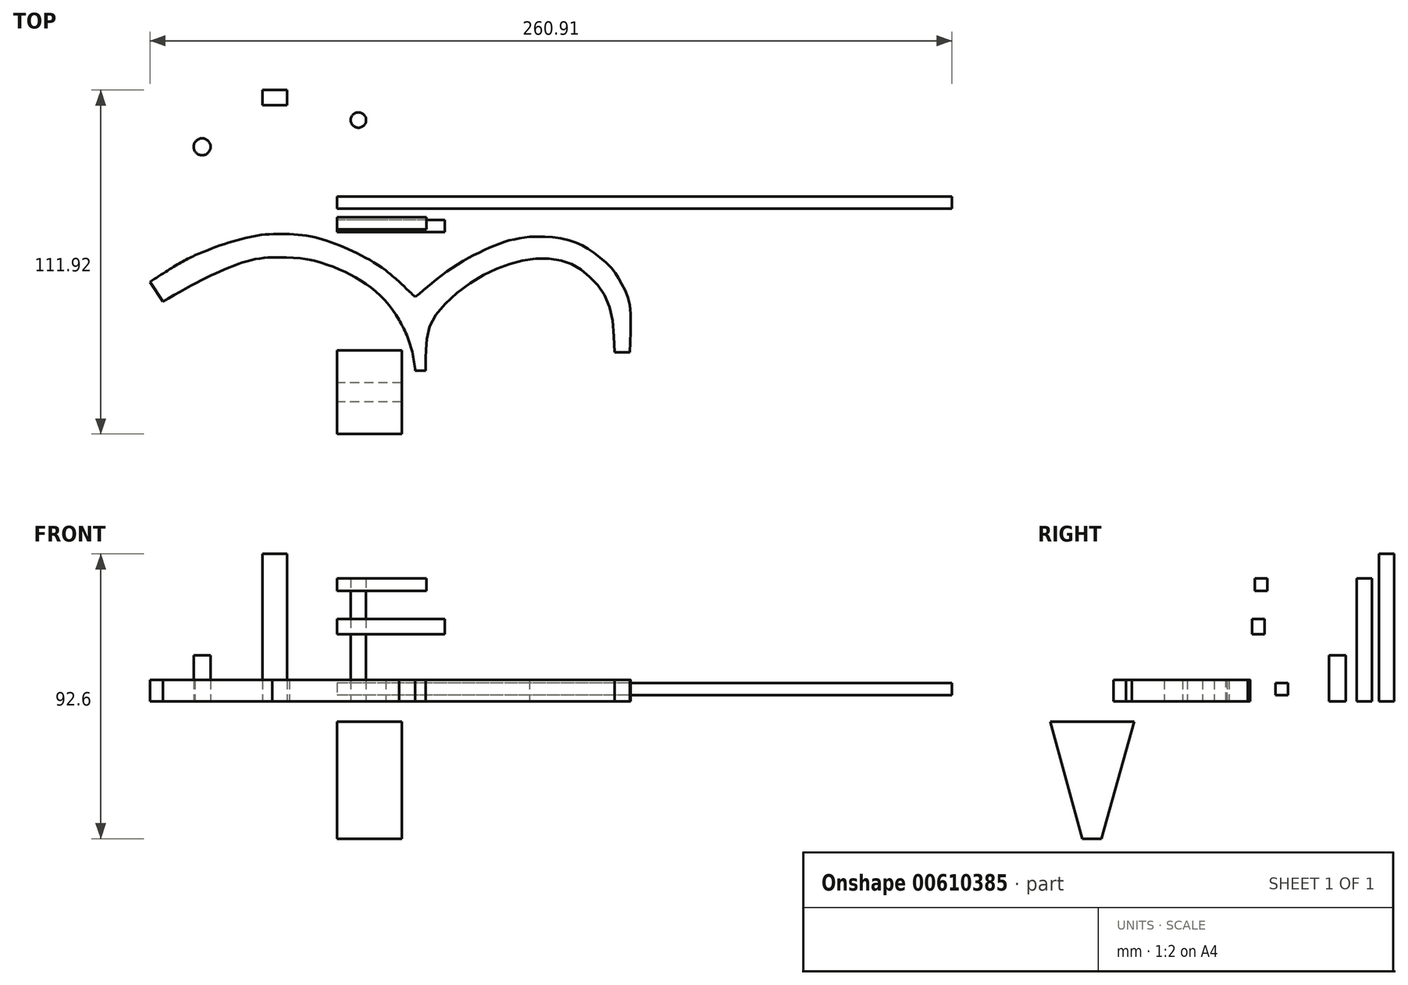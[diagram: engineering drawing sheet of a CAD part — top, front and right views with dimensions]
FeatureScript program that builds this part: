
annotation { "Feature Type Name" : "Feature", "Feature Type Description" : "" }
export const myFeature = defineFeature(function(context is Context, id is Id, definition is map)
    precondition{}
    {
        {
            var Q0;
            Q0=qCreatedBy(makeId("Top.planeOp"),FACE);
            var sketch = newSketch(context, id + "F0", { "sketchPlane" : qUnion([Q0])});
            skFitSpline(sketch, "E0", {"points": [v(-60.91, -6.53) * mm, v(-54.5, -2.45) * mm, v(-50.14, 0.16) * mm, v(-46.25, 2.14) * mm], "startDerivative": vector(16.01, 10.57) * mm, "endDerivative": vector(13, 6.35) * mm});
            skFitSpline(sketch, "E1", {"points": [v(-46.25, 2.14) * mm, v(-37.97, 5.34) * mm, v(-29.58, 7.82) * mm, v(-22.67, 8.93) * mm, v(-15.55, 8.98) * mm], "startDerivative": vector(30.88, 12.56) * mm, "endDerivative": vector(30.39, -0.7) * mm});
            skFitSpline(sketch, "E2", {"points": [v(-15.55, 8.98) * mm, v(-9.55, 8.46) * mm, v(-3.97, 7.07) * mm, v(2.6, 4.6) * mm, v(9.53, 1.22) * mm, v(15.8, -2.7) * mm], "startDerivative": vector(32.42, -1.74) * mm, "endDerivative": vector(29.3, -20.88) * mm});
            skFitSpline(sketch, "E3", {"points": [v(15.8, -2.7) * mm, v(20.28, -6.6) * mm, v(25.42, -11.43) * mm], "startDerivative": vector(8.02, -7.35) * mm, "endDerivative": vector(10.95, -9.58) * mm});
            skFitSpline(sketch, "E4", {"points": [v(25.42, -11.43) * mm, v(31.57, -6.35) * mm, v(40.36, -0.1) * mm, v(48.65, 4.16) * mm, v(55.71, 6.87) * mm, v(62.61, 8.1) * mm], "startDerivative": vector(29.98, 25.4) * mm, "endDerivative": vector(38.2, 5.06) * mm});
            skFitSpline(sketch, "E5", {"points": [v(62.61, 8.1) * mm, v(68.78, 8.1) * mm, v(75.88, 6.87) * mm, v(80.74, 4.76) * mm, v(85.37, 1.55) * mm, v(89.92, -2.86) * mm, v(92.1, -6.3) * mm, v(94.56, -11.43) * mm, v(95.53, -18.9) * mm, v(95.15, -29.45) * mm], "startDerivative": vector(54.77, 2.08) * mm, "endDerivative": vector(-4.35, -75.98) * mm});
            skFitSpline(sketch, "E6", {"points": [v(95.15, -29.45) * mm, v(90.25, -29.45) * mm], "startDerivative": vector(-4.9, 0) * mm, "endDerivative": vector(-4.9, 0) * mm});
            skFitSpline(sketch, "E7", {"points": [v(90.25, -29.45) * mm, v(89.33, -17.69) * mm, v(86.4, -9.82) * mm, v(82.07, -4.8) * mm, v(77.2, -1.17) * mm, v(71.73, 0.68) * mm, v(63.32, 0.91) * mm, v(55.06, -1.1) * mm, v(45.82, -5.22) * mm, v(35.84, -13.06) * mm, v(30.28, -20.62) * mm, v(28.97, -27.65) * mm, v(28.74, -31.35) * mm], "startDerivative": vector(-3.52, 121.43) * mm, "endDerivative": vector(-3.24, -59.77) * mm});
            skFitSpline(sketch, "E8", {"points": [v(28.74, -31.35) * mm, v(28.8, -35.47) * mm], "startDerivative": vector(0.06, -4.12) * mm, "endDerivative": vector(0.06, -4.12) * mm});
            skFitSpline(sketch, "E9", {"points": [v(28.8, -35.47) * mm, v(25.42, -35.47) * mm], "startDerivative": vector(-3.38, 0) * mm, "endDerivative": vector(-3.38, 0) * mm});
            skFitSpline(sketch, "E10", {"points": [v(25.42, -35.47) * mm, v(24.48, -29.45) * mm, v(22.31, -23.1) * mm, v(20.16, -18.9) * mm], "startDerivative": vector(-1.93, 17.27) * mm, "endDerivative": vector(-6.87, 12.9) * mm});
            skFitSpline(sketch, "E11", {"points": [v(20.16, -18.9) * mm, v(15.05, -11.97) * mm, v(7.89, -6.23) * mm, v(0.52, -2.38) * mm, v(-9.7, 0.8) * mm, v(-21.13, 1.47) * mm], "startDerivative": vector(-24.14, 38.09) * mm, "endDerivative": vector(-53.27, -0.14) * mm});
            skFitSpline(sketch, "E12", {"points": [v(-21.13, 1.47) * mm, v(-27.74, 0.65) * mm, v(-35.5, -2) * mm, v(-43.87, -5.79) * mm, v(-56.74, -12.96) * mm], "startDerivative": vector(-31, -2.16) * mm, "endDerivative": vector(-43.46, -25.1) * mm});
            skLineSegment(sketch, "E13", {"start": v(-72.72, -62.87) * mm, "end": v(27.19, -67.17) * mm});
            skLineSegment(sketch, "E14", {"start": v(-60.91, -6.53) * mm, "end": v(-56.74, -12.96) * mm});
            skSolve(sketch);
        }
        {
            var Q0;
            Q0=qCreatedBy(makeId("Top.planeOp"),FACE);
            var sketch = newSketch(context, id + "F1", { "sketchPlane" : qUnion([Q0])});
            skCircle(sketch, "E15", {"center": v(-43.93, 37.41) * mm, "radius": 2.75 * mm});
            skSolve(sketch);
        }
        {
            var Q0;
            Q0=makeQuery(id+"F0.imprint","IMPRINT",FACE,{"disambiguationData":[TD([[makeQuery(id+"F0.imprint","IMPRINT",EDGE,{"derivedFrom":sQuery(id+"F0.wireOp",EDGE,"E0")}),-1.0]])]});
            extrude(context, id + "F2", {"entities" : qUnion([Q0]), "flatOperationType" : FlatOperationType.REMOVE, "depth" : 7 * mm, "offsetDistance" : 25 * mm, "domain" : OperationDomain.MODEL});
        }
        {
            var Q0;
            Q0=qCreatedBy(makeId("Top.planeOp"),FACE);
            var sketch = newSketch(context, id + "F3", { "sketchPlane" : qUnion([Q0])});
            skLineSegment(sketch, "E16.bottom", {"start": v(-24.3, 55.9) * mm, "end": v(-16.3, 55.9) * mm});
            skLineSegment(sketch, "E16.top", {"start": v(-24.3, 50.9) * mm, "end": v(-16.3, 50.9) * mm});
            skLineSegment(sketch, "E16.left", {"start": v(-24.3, 55.9) * mm, "end": v(-24.3, 50.9) * mm});
            skLineSegment(sketch, "E16.right", {"start": v(-16.3, 55.9) * mm, "end": v(-16.3, 50.9) * mm});
            skSolve(sketch);
        }
        {
            var Q0;
            Q0 = qSketchRegion(id + "F3", true);
            extrude(context, id + "F4", {"entities" : qUnion([Q0]), "depth" : 48 * mm, "offsetDistance" : 25 * mm});
        }
        {
            var Q0;
            Q0=qCreatedBy(makeId("Top.planeOp"),FACE);
            var sketch = newSketch(context, id + "F5", { "sketchPlane" : qUnion([Q0])});
            skCircle(sketch, "E17", {"center": v(6.92, 46.1) * mm, "radius": 2.5 * mm});
            skSolve(sketch);
        }
        {
            var Q0;
            Q0 = qSketchRegion(id + "F5", true);
            extrude(context, id + "F6", {"entities" : qUnion([Q0]), "depth" : 40 * mm, "offsetDistance" : 25 * mm});
        }
        {
            var Q0;
            Q0 = qSketchRegion(id + "F1", true);
            extrude(context, id + "F7", {"entities" : qUnion([Q0]), "depth" : 15 * mm, "offsetDistance" : 25 * mm});
        }
        {
            var Q0;
            Q0=qCreatedBy(makeId("Right.planeOp"),FACE);
            var sketch = newSketch(context, id + "F8", { "sketchPlane" : qUnion([Q0])});
            skLineSegment(sketch, "E18", {"start": v(-56.03, -6.5) * mm, "end": v(-28.78, -6.5) * mm});
            skLineSegment(sketch, "E19", {"start": v(-28.78, -6.5) * mm, "end": v(-39.36, -44.6) * mm});
            skLineSegment(sketch, "E20", {"start": v(-39.36, -44.6) * mm, "end": v(-45.57, -44.6) * mm});
            skLineSegment(sketch, "E21", {"start": v(-45.57, -44.6) * mm, "end": v(-56.03, -6.5) * mm});
            skSolve(sketch);
        }
        {
            var Q0;
            Q0 = qSketchRegion(id + "F8", true);
            extrude(context, id + "F9", {"entities" : qUnion([Q0]), "depth" : 21 * mm, "offsetDistance" : 25 * mm});
        }
        {
            var Q0;
            Q0=qCreatedBy(makeId("Right.planeOp"),FACE);
            var sketch = newSketch(context, id + "F10", { "sketchPlane" : qUnion([Q0])});
            skLineSegment(sketch, "E22.bottom", {"start": v(17.26, 6.03) * mm, "end": v(21.26, 6.03) * mm});
            skLineSegment(sketch, "E22.top", {"start": v(17.26, 2.03) * mm, "end": v(21.26, 2.03) * mm});
            skLineSegment(sketch, "E22.left", {"start": v(17.26, 6.03) * mm, "end": v(17.26, 2.03) * mm});
            skLineSegment(sketch, "E22.right", {"start": v(21.26, 6.03) * mm, "end": v(21.26, 2.03) * mm});
            skSolve(sketch);
        }
        {
            var Q0;
            Q0 = qSketchRegion(id + "F10", true);
            extrude(context, id + "F11", {"entities" : qUnion([Q0]), "depth" : 200 * mm, "offsetDistance" : 25 * mm});
        }
        {
            var Q0;
            Q0=qCreatedBy(makeId("Right.planeOp"),FACE);
            var sketch = newSketch(context, id + "F12", { "sketchPlane" : qUnion([Q0])});
            skLineSegment(sketch, "E23.bottom", {"start": v(16.87, 12.5) * mm, "end": v(20.87, 12.5) * mm});
            skLineSegment(sketch, "E23.top", {"start": v(16.87, 8.5) * mm, "end": v(20.87, 8.5) * mm});
            skLineSegment(sketch, "E23.left", {"start": v(16.87, 12.5) * mm, "end": v(16.87, 8.5) * mm});
            skLineSegment(sketch, "E23.right", {"start": v(20.87, 12.5) * mm, "end": v(20.87, 8.5) * mm});
            skSolve(sketch);
        }
        {
            var Q0;
            Q0=qCreatedBy(makeId("Right.planeOp"),FACE);
            var sketch = newSketch(context, id + "F13", { "sketchPlane" : qUnion([Q0])});
            skLineSegment(sketch, "E24.bottom", {"start": v(9.67, 26.88) * mm, "end": v(13.67, 26.88) * mm});
            skLineSegment(sketch, "E24.top", {"start": v(9.67, 21.88) * mm, "end": v(13.67, 21.88) * mm});
            skLineSegment(sketch, "E24.left", {"start": v(9.67, 26.88) * mm, "end": v(9.67, 21.88) * mm});
            skLineSegment(sketch, "E24.right", {"start": v(13.67, 26.88) * mm, "end": v(13.67, 21.88) * mm});
            skSolve(sketch);
        }
        {
            var Q0;
            Q0 = qSketchRegion(id + "F13", true);
            extrude(context, id + "F14", {"entities" : qUnion([Q0]), "depth" : 35 * mm, "offsetDistance" : 25 * mm});
        }
        {
            var Q0;
            Q0=qCreatedBy(makeId("Right.planeOp"),FACE);
            var sketch = newSketch(context, id + "F15", { "sketchPlane" : qUnion([Q0])});
            skLineSegment(sketch, "E25.bottom", {"start": v(10.52, 40.04) * mm, "end": v(14.52, 40.04) * mm});
            skLineSegment(sketch, "E25.top", {"start": v(10.52, 36.04) * mm, "end": v(14.52, 36.04) * mm});
            skLineSegment(sketch, "E25.left", {"start": v(10.52, 40.04) * mm, "end": v(10.52, 36.04) * mm});
            skLineSegment(sketch, "E25.right", {"start": v(14.52, 40.04) * mm, "end": v(14.52, 36.04) * mm});
            skSolve(sketch);
        }
        {
            var Q0;
            Q0 = qSketchRegion(id + "F15", true);
            extrude(context, id + "F16", {"entities" : qUnion([Q0]), "depth" : 29 * mm, "offsetDistance" : 25 * mm});
        }
    });
